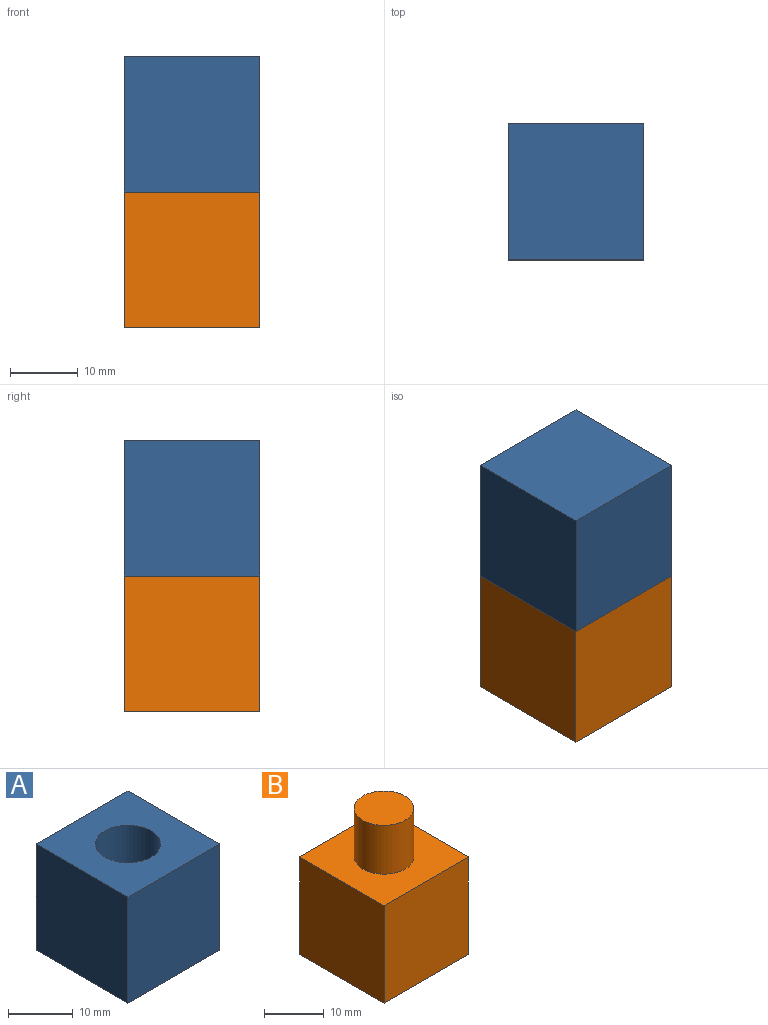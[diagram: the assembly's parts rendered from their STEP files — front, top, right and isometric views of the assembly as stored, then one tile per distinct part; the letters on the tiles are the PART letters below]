
ASSEMBLY  parts=2 mates=1
PART A: 8 faces, bbox 20x20x20 mm
  f0: plane 20x20mm, normal (1,0,0), area 400mm2, adj f1,f3,f4,f5
  f1: plane 20x20mm, normal (0,1,0), area 400mm2, adj f0,f2,f4,f5
  f2: plane 20x20mm, normal (-1,0,0), area 400mm2, adj f1,f3,f4,f5
  f3: plane 20x20mm, normal (0,-1,0), area 400mm2, adj f0,f2,f4,f5
  f4: plane 20x20mm, normal (0,0,1), area 321.5mm2, adj f0,f1,f2,f3,f6
  f5: plane 20x20mm, normal (0,0,-1), area 400mm2, adj f0,f1,f2,f3
  f6: cylinder r=5mm len=10mm, axis (0,0,1), area 314.2mm2, adj f4,f7
  f7: plane 10x10mm, normal (0,0,1), area 78.5mm2, adj f6
PART B: 8 faces, bbox 20x20x30 mm
  f0: plane 20x20mm, normal (1,0,0), area 400mm2, adj f1,f3,f4,f5
  f1: plane 20x20mm, normal (0,1,0), area 400mm2, adj f0,f2,f4,f5
  f2: plane 20x20mm, normal (-1,0,0), area 400mm2, adj f1,f3,f4,f5
  f3: plane 20x20mm, normal (0,-1,0), area 400mm2, adj f0,f2,f4,f5
  f4: plane 20x20mm, normal (0,0,1), area 321.5mm2, adj f0,f1,f2,f3,f6
  f5: plane 20x20mm, normal (0,0,-1), area 400mm2, adj f0,f1,f2,f3
  f6: cylinder r=5mm len=10mm, axis (0,0,-1), area 314.2mm2, adj f4,f7
  f7: plane 10x10mm, normal (0,0,1), area 78.5mm2, adj f6
PLACE A rot(axis=(0.71,-0.71,0),180deg) t=(19.2,18.98,48.06)mm
PLACE B t=(19.2,18.98,8.06)mm
MATE slider A.f4 <-> B.f4  axis (0,0,1) through (-0.8,18.98,28.06)mm
